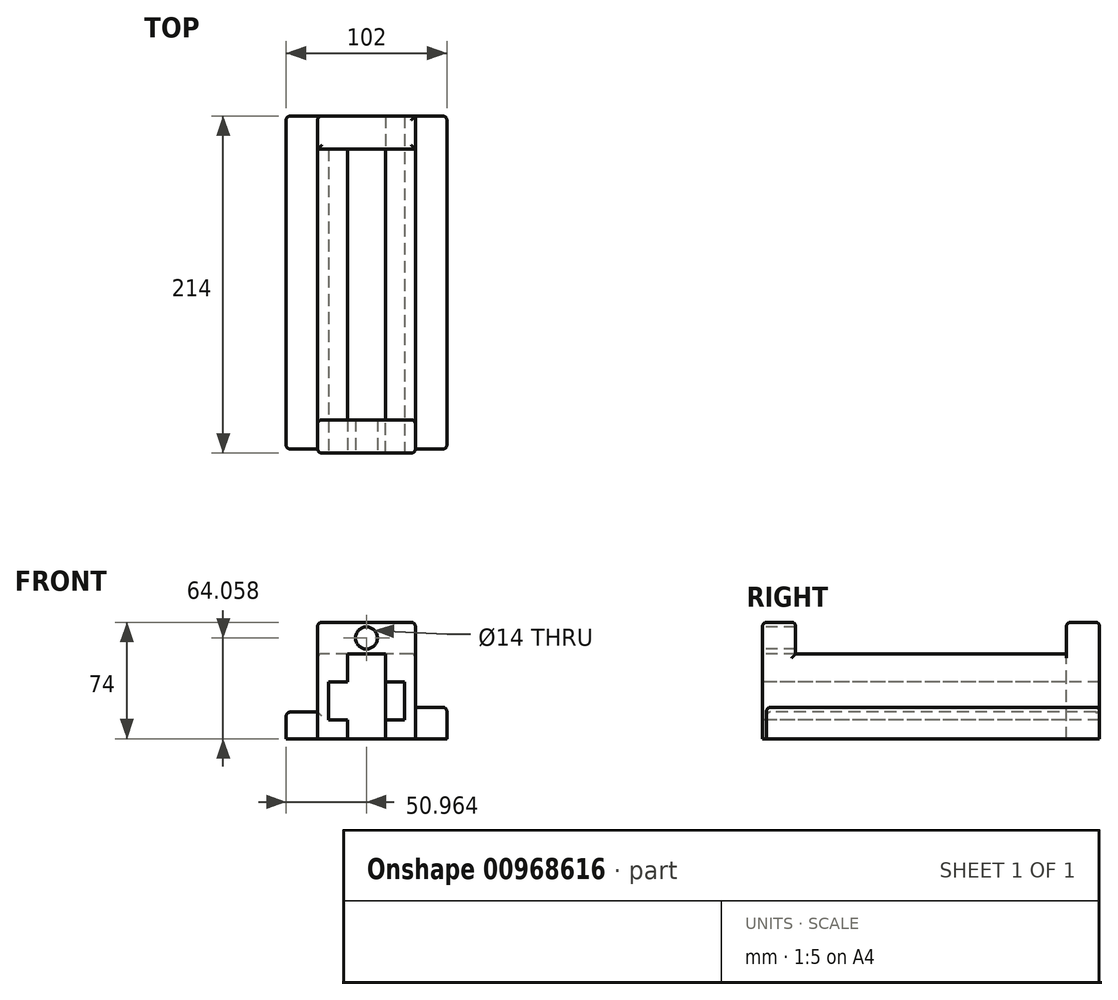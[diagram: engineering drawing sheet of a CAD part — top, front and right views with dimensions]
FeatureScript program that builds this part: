
annotation { "Feature Type Name" : "Feature", "Feature Type Description" : "" }
export const myFeature = defineFeature(function(context is Context, id is Id, definition is map)
    precondition{}
    {
        {
            var Q0;
            Q0=qCreatedBy(makeId("Front.planeOp"),FACE);
            var sketch = newSketch(context, id + "F0", { "sketchPlane" : qUnion([Q0])});
            skLineSegment(sketch, "E0", {"start": v(0, 0) * mm, "end": v(-19, 0) * mm});
            skLineSegment(sketch, "E1", {"start": v(-19, 0) * mm, "end": v(-19, 54) * mm});
            skLineSegment(sketch, "E2", {"start": v(-19, 54) * mm, "end": v(43, 54) * mm});
            skLineSegment(sketch, "E3", {"start": v(43, 54) * mm, "end": v(43, 0) * mm});
            skLineSegment(sketch, "E4", {"start": v(43, 0) * mm, "end": v(24, 0) * mm});
            skLineSegment(sketch, "E5", {"start": v(24, 0) * mm, "end": v(24, 12) * mm});
            skLineSegment(sketch, "E6", {"start": v(24, 12) * mm, "end": v(36, 12) * mm});
            skLineSegment(sketch, "E7", {"start": v(36, 12) * mm, "end": v(36, 24) * mm});
            skLineSegment(sketch, "E8", {"start": v(0, 0) * mm, "end": v(0, 12) * mm});
            skLineSegment(sketch, "E9", {"start": v(0, 12) * mm, "end": v(-12, 12) * mm});
            skLineSegment(sketch, "E10", {"start": v(-12, 12) * mm, "end": v(-12, 24) * mm});
            skLineSegment(sketch, "E11", {"start": v(-12, 24) * mm, "end": v(0, 24) * mm});
            skLineSegment(sketch, "E12", {"start": v(0, 24) * mm, "end": v(0, 36) * mm});
            skLineSegment(sketch, "E13", {"start": v(0, 36) * mm, "end": v(24, 36) * mm});
            skLineSegment(sketch, "E14", {"start": v(24, 36) * mm, "end": v(24, 24) * mm});
            skLineSegment(sketch, "E15", {"start": v(24, 24) * mm, "end": v(36, 24) * mm});
            skSolve(sketch);
        }
        {
            var Q0;
            Q0=makeQuery(id+"F0.imprint","IMPRINT",FACE,{"disambiguationData":[TD([[makeQuery(id+"F0.imprint","IMPRINT",EDGE,{"derivedFrom":sQuery(id+"F0.wireOp",EDGE,"E0")}),-1.0]])]});
            extrude(context, id + "F1", {"entities" : qUnion([Q0]), "oppositeDirection" : true, "depth" : 214 * mm, "offsetDistance" : 25 * mm});
        }
        {
            var Q0;
            Q0=makeQuery(id+"F1.opExtrude","CAP_FACE",FACE,{"disambiguationData":[OSD([sQuery(id+"F0.wireOp",EDGE,"E0"),sQuery(id+"F0.wireOp",EDGE,"E1"),sQuery(id+"F0.wireOp",EDGE,"E2"),sQuery(id+"F0.wireOp",EDGE,"E3"),sQuery(id+"F0.wireOp",EDGE,"E4"),sQuery(id+"F0.wireOp",EDGE,"E5"),sQuery(id+"F0.wireOp",EDGE,"E6"),sQuery(id+"F0.wireOp",EDGE,"E7"),sQuery(id+"F0.wireOp",EDGE,"E8"),sQuery(id+"F0.wireOp",EDGE,"E9"),sQuery(id+"F0.wireOp",EDGE,"E10"),sQuery(id+"F0.wireOp",EDGE,"E11"),sQuery(id+"F0.wireOp",EDGE,"E12"),sQuery(id+"F0.wireOp",EDGE,"E13"),sQuery(id+"F0.wireOp",EDGE,"E14"),sQuery(id+"F0.wireOp",EDGE,"E15")])],"isStart":false});
            var sketch = newSketch(context, id + "F2", { "sketchPlane" : qUnion([Q0])});
            skLineSegment(sketch, "E16.bottom", {"start": v(-24, 0) * mm, "end": v(0, 0) * mm});
            skLineSegment(sketch, "E16.top", {"start": v(-24, 36) * mm, "end": v(0, 36) * mm});
            skLineSegment(sketch, "E16.left", {"start": v(-24, 0) * mm, "end": v(-24, 36) * mm});
            skLineSegment(sketch, "E16.right", {"start": v(0, 0) * mm, "end": v(0, 36) * mm});
            skLineSegment(sketch, "E17.bottom", {"start": v(-24, 12) * mm, "end": v(-36, 12) * mm});
            skLineSegment(sketch, "E17.top", {"start": v(-24, 12) * mm, "end": v(-36, 12) * mm});
            skLineSegment(sketch, "E17.left", {"start": v(-24, 12) * mm, "end": v(-24, 12) * mm});
            skLineSegment(sketch, "E17.right", {"start": v(-36, 12) * mm, "end": v(-36, 12) * mm});
            skSolve(sketch);
        }
        {
            var Q0;
            {var subQ0=sQuery(id+"F2.wireOp",EDGE,"E17.top");Q0=makeQuery(id+"F2.imprint","IMPRINT",FACE,{"disambiguationData":[TD([[makeQuery(id+"F2.imprint","IMPRINT",EDGE,{"derivedFrom":subQ0}),-1.0]])]});}
            var Q1;
            {var subQ3=sQuery(id+"F2.wireOp",EDGE,"E16.bottom");Q1=makeQuery(id+"F2.imprint","IMPRINT",FACE,{"disambiguationData":[TD([[makeQuery(id+"F2.imprint","IMPRINT",EDGE,{"derivedFrom":subQ3}),1.0]])]});}
            var Q2;
            {var subQ1=makeQuery(id+"F1.opExtrude","CAP_EDGE",EDGE,{"disambiguationData":[OSD([sQuery(id+"F0.wireOp",EDGE,"E9")])],"isStart":false});Q2=makeQuery(id+"F2.imprint","IMPRINT",FACE,{"disambiguationData":[TD([[makeQuery(id+"F2.imprint","IMPRINT",EDGE,{"derivedFrom":subQ1}),1.0]])]});}
            extrude(context, id + "F3", {"entities" : qUnion([Q0, Q1, Q2]), "operationType" : NewBodyOperationType.ADD, "oppositeDirection" : true, "depth" : 21 * mm, "offsetDistance" : 25 * mm});
        }
        {
            var Q0;
            Q0=makeQuery(id+"F1.opExtrude","SWEPT_FACE",FACE,{"disambiguationData":[OSD([sQuery(id+"F0.wireOp",EDGE,"E2")])]});
            var sketch = newSketch(context, id + "F4", { "sketchPlane" : qUnion([Q0])});
            skLineSegment(sketch, "E18", {"start": v(43, 0) * mm, "end": v(24, 0) * mm});
            skLineSegment(sketch, "E19", {"start": v(24, 0) * mm, "end": v(24, 214) * mm});
            skLineSegment(sketch, "E20", {"start": v(-19, 0) * mm, "end": v(0, 0) * mm});
            skLineSegment(sketch, "E21", {"start": v(0, 0) * mm, "end": v(0, 214) * mm});
            skSolve(sketch);
        }
        {
            var Q0;
            {var subQ0=sQuery(id+"F4.wireOp",EDGE,"E19");Q0=makeQuery(id+"F4.imprint","IMPRINT",FACE,{"disambiguationData":[TD([[makeQuery(id+"F4.imprint","IMPRINT",EDGE,{"derivedFrom":subQ0}),1.0]])]});}
            extrude(context, id + "F5", {"entities" : qUnion([Q0]), "operationType" : NewBodyOperationType.REMOVE, "oppositeDirection" : true, "depth" : 20.2 * mm, "offsetDistance" : 25 * mm});
        }
        {
            var Q0;
            {var subQ1=sQuery(id+"F0.wireOp",EDGE,"E1");var subQ14=sQuery(id+"F0.wireOp",EDGE,"E2");Q0=makeQuery(id+"F5.boolean.opBoolean","SPLIT",FACE,{"disambiguationData":[TD([makeQuery(id+"F1.opExtrude","SWEPT_FACE",FACE,{"disambiguationData":[OSD([subQ1])]})])],"derivedFrom":makeQuery(id+"F1.opExtrude","SWEPT_FACE",FACE,{"disambiguationData":[OSD([subQ14])]})});}
            var sketch = newSketch(context, id + "F6", { "sketchPlane" : qUnion([Q0])});
            skLineSegment(sketch, "E22", {"start": v(0, 214) * mm, "end": v(0, 193) * mm});
            skLineSegment(sketch, "E23", {"start": v(0, 193) * mm, "end": v(-19, 193) * mm});
            skSolve(sketch);
        }
        {
            var Q0;
            Q0=makeQuery(id+"F5.boolean.opBoolean","COPY",FACE,{"derivedFrom":makeQuery(id+"F5.opExtrude","CAP_FACE",FACE,{"disambiguationData":[OSD([sQuery(id+"F0.wireOp",EDGE,"E2"),sQuery(id+"F4.wireOp",EDGE,"E19"),sQuery(id+"F4.wireOp",EDGE,"E21")])],"isStart":false})});
            extrude(context, id + "F7", {"entities" : qUnion([Q0]), "operationType" : NewBodyOperationType.ADD, "depth" : 40 * mm, "offsetDistance" : 25 * mm});
        }
        {
            var Q0;
            Q0=makeQuery(id+"F6.imprint","IMPRINT",FACE,{"disambiguationData":[TD([[makeQuery(id+"F6.imprint","IMPRINT",EDGE,{"derivedFrom":sQuery(id+"F6.wireOp",EDGE,"E22")}),1.0]])]});
            extrude(context, id + "F8", {"entities" : qUnion([Q0]), "operationType" : NewBodyOperationType.ADD, "depth" : 20 * mm, "offsetDistance" : 25 * mm});
        }
        {
            var Q0;
            Q0=makeQuery(id+"F7.opExtrude","SWEPT_FACE",FACE,{"disambiguationData":[OSD([sQuery(id+"F4.wireOp",EDGE,"E19")])]});
            extrude(context, id + "F9", {"entities" : qUnion([Q0]), "operationType" : NewBodyOperationType.ADD, "depth" : 19 * mm, "offsetDistance" : 25 * mm});
        }
        {
            var Q0;
            Q0=makeQuery(id+"F1.opExtrude","SWEPT_FACE",FACE,{"disambiguationData":[OSD([sQuery(id+"F0.wireOp",EDGE,"E11")])]});
            var Q1;
            Q1=makeQuery(id+"F1.opExtrude","SWEPT_FACE",FACE,{"disambiguationData":[OSD([sQuery(id+"F0.wireOp",EDGE,"E15")])]});
            extrude(context, id + "F10", {"entities" : qUnion([Q0, Q1]), "operationType" : NewBodyOperationType.REMOVE, "oppositeDirection" : true, "depth" : 12 * mm, "offsetDistance" : 25 * mm});
        }
        {
            var Q0;
            {var subQ1=sQuery(id+"F0.wireOp",EDGE,"E1");var subQ14=sQuery(id+"F0.wireOp",EDGE,"E2");Q0=makeQuery(id+"F5.boolean.opBoolean","SPLIT",FACE,{"disambiguationData":[TD([makeQuery(id+"F1.opExtrude","SWEPT_FACE",FACE,{"disambiguationData":[OSD([subQ1])]})])],"derivedFrom":makeQuery(id+"F1.opExtrude","SWEPT_FACE",FACE,{"disambiguationData":[OSD([subQ14])]})});}
            var sketch = newSketch(context, id + "F11", { "sketchPlane" : qUnion([Q0])});
            skLineSegment(sketch, "E24", {"start": v(-19, 0) * mm, "end": v(-19, 21) * mm});
            skLineSegment(sketch, "E25", {"start": v(-19, 21) * mm, "end": v(0, 21) * mm});
            skSolve(sketch);
        }
        {
            var Q0;
            Q0=makeQuery(id+"F11.imprint","IMPRINT",FACE,{"disambiguationData":[TD([[makeQuery(id+"F11.imprint","IMPRINT",EDGE,{"derivedFrom":sQuery(id+"F11.wireOp",EDGE,"E24")}),1.0]])]});
            extrude(context, id + "F12", {"entities" : qUnion([Q0]), "operationType" : NewBodyOperationType.ADD, "depth" : 20 * mm, "offsetDistance" : 25 * mm});
        }
        {
            var Q0;
            {var subQ0=sQuery(id+"F4.wireOp",EDGE,"E19");Q0=makeQuery(id+"F9.boolean.opBoolean","MERGE",FACE,{"derivedFrom":[makeQuery(id+"F7.opExtrude","CAP_FACE",FACE,{"disambiguationData":[OSD([sQuery(id+"F0.wireOp",EDGE,"E2"),subQ0,sQuery(id+"F4.wireOp",EDGE,"E21")])],"isStart":false}),makeQuery(id+"F9.opExtrude","SWEPT_FACE",FACE,{"disambiguationData":[OSD([subQ0]),TDD([makeQuery(id+"F7.opExtrude","CAP_EDGE",EDGE,{"disambiguationData":[OSD([subQ0])],"isStart":false})])]})]});}
            extrude(context, id + "F13", {"entities" : qUnion([Q0]), "operationType" : NewBodyOperationType.ADD, "depth" : 0.2 * mm, "offsetDistance" : 25 * mm});
        }
        {
            var Q0;
            {var subQ0=sQuery(id+"F4.wireOp",EDGE,"E21");Q0=makeQuery(id+"F12.boolean.opBoolean","MERGE",FACE,{"derivedFrom":[makeQuery(id+"F5.boolean.opBoolean","MERGE",FACE,{"derivedFrom":[makeQuery(id+"F1.opExtrude","SWEPT_FACE",FACE,{"disambiguationData":[OSD([sQuery(id+"F0.wireOp",EDGE,"E12")])]})],"fromTools":[makeQuery(id+"F5.opExtrude","SWEPT_FACE",FACE,{"disambiguationData":[OSD([subQ0])]})]}),makeQuery(id+"F12.opExtrude","SWEPT_FACE",FACE,{"disambiguationData":[OSD([subQ0])]})]});}
            var sketch = newSketch(context, id + "F14", { "sketchPlane" : qUnion([Q0])});
            skLineSegment(sketch, "E26", {"start": v(21, 54) * mm, "end": v(0, 54) * mm});
            skSolve(sketch);
        }
        {
            var Q0;
            {var subQ0=sQuery(id+"F14.wireOp",EDGE,"E26");Q0=makeQuery(id+"F14.imprint","IMPRINT",FACE,{"disambiguationData":[TD([[makeQuery(id+"F14.imprint","IMPRINT",EDGE,{"derivedFrom":subQ0}),-1.0]])]});}
            extrude(context, id + "F15", {"entities" : qUnion([Q0]), "operationType" : NewBodyOperationType.ADD, "depth" : 43 * mm, "offsetDistance" : 25 * mm});
        }
        {
            var Q0;
            {var subQ0=sQuery(id+"F4.wireOp",EDGE,"E21");var subQ1=sQuery(id+"F0.wireOp",EDGE,"E12");var subQ2=sQuery(id+"F0.wireOp",EDGE,"E2");var subQ3=sQuery(id+"F0.wireOp",EDGE,"E11");var subQ6=sQuery(id+"F0.wireOp",EDGE,"E10");var subQ7=sQuery(id+"F0.wireOp",EDGE,"E8");var subQ8=sQuery(id+"F0.wireOp",EDGE,"E9");var subQ9=sQuery(id+"F0.wireOp",EDGE,"E0");var subQ11=sQuery(id+"F0.wireOp",EDGE,"E1");var subQ12=sQuery(id+"F0.wireOp",EDGE,"E4");var subQ14=sQuery(id+"F0.wireOp",EDGE,"E15");var subQ15=sQuery(id+"F0.wireOp",EDGE,"E14");var subQ16=sQuery(id+"F0.wireOp",EDGE,"E7");var subQ17=sQuery(id+"F0.wireOp",EDGE,"E6");var subQ18=sQuery(id+"F0.wireOp",EDGE,"E5");var subQ19=sQuery(id+"F0.wireOp",EDGE,"E3");var subQ20=makeQuery(id+"F1.opExtrude","CAP_FACE",FACE,{"disambiguationData":[OSD([subQ9,subQ11,subQ2,subQ19,subQ12,subQ18,subQ17,subQ16,subQ7,subQ8,subQ6,subQ3,subQ1,sQuery(id+"F0.wireOp",EDGE,"E13"),subQ15,subQ14])],"isStart":true});Q0=makeQuery(id+"F15.boolean.opBoolean","MERGE",FACE,{"derivedFrom":[makeQuery(id+"F5.boolean.opBoolean","SPLIT",FACE,{"disambiguationData":[TD([makeQuery(id+"F1.opExtrude","SWEPT_FACE",FACE,{"disambiguationData":[OSD([subQ19])]})])],"derivedFrom":subQ20}),makeQuery(id+"F12.boolean.opBoolean","MERGE",FACE,{"derivedFrom":[makeQuery(id+"F5.boolean.opBoolean","SPLIT",FACE,{"disambiguationData":[TD([makeQuery(id+"F1.opExtrude","SWEPT_FACE",FACE,{"disambiguationData":[OSD([subQ11])]})])],"derivedFrom":subQ20}),makeQuery(id+"F12.opExtrude","SWEPT_FACE",FACE,{"disambiguationData":[OSD([subQ2])]})]}),makeQuery(id+"F15.opExtrude","SWEPT_FACE",FACE,{"disambiguationData":[OSD([subQ2,subQ1,sQuery(id+"F4.wireOp",EDGE,"E20"),subQ0])]})]});}
            var sketch = newSketch(context, id + "F16", { "sketchPlane" : qUnion([Q0])});
            skSolve(sketch);
        }
        {
            var Q0;
            {var subQ1=sQuery(id+"F0.wireOp",EDGE,"E2");var subQ5=sQuery(id+"F4.wireOp",EDGE,"E21");var subQ6=sQuery(id+"F4.wireOp",EDGE,"E20");var subQ7=sQuery(id+"F0.wireOp",EDGE,"E12");var subQ13=makeQuery(id+"F15.boolean.opBoolean","MERGE",EDGE,{"derivedFrom":[makeQuery(id+"F12.opExtrude","CAP_EDGE",EDGE,{"disambiguationData":[OSD([subQ1])],"isStart":false}),makeQuery(id+"F15.opExtrude","SWEPT_EDGE",EDGE,{"disambiguationData":[OSD([subQ1,subQ7,subQ6,subQ5])]})]});Q0=makeQuery(id+"F16.imprint","IMPRINT",FACE,{"disambiguationData":[TD([[makeQuery(id+"F16.imprint","IMPRINT",EDGE,{"derivedFrom":subQ13}),-1.0]])]});}
            var sketch = newSketch(context, id + "F17", { "sketchPlane" : qUnion([Q0])});
            skCircle(sketch, "E27", {"center": v(11.96, 64.06) * mm, "radius": 7 * mm});
            skSolve(sketch);
        }
        {
            var Q0;
            Q0=makeQuery(id+"F17.imprint","IMPRINT",FACE,{"disambiguationData":[TD([[makeQuery(id+"F17.imprint","IMPRINT",EDGE,{"derivedFrom":sQuery(id+"F17.wireOp",EDGE,"E27")}),1.0]])]});
            extrude(context, id + "F18", {"entities" : qUnion([Q0]), "operationType" : NewBodyOperationType.REMOVE, "oppositeDirection" : true, "depth" : 69.1 * mm, "offsetDistance" : 25 * mm});
        }
        {
            var Q0;
            Q0=makeQuery(id+"F16.imprint","IMPRINT",FACE,{"disambiguationData":[TD([[makeQuery(id+"F16.imprint","IMPRINT",EDGE,{"derivedFrom":makeQuery(id+"F1.opExtrude","CAP_EDGE",EDGE,{"disambiguationData":[OSD([sQuery(id+"F0.wireOp",EDGE,"E0")])],"isStart":true})}),-1.0]])]});
            var sketch = newSketch(context, id + "F19", { "sketchPlane" : qUnion([Q0])});
            skSolve(sketch);
        }
        {
            var Q0;
            Q0=makeQuery(id+"F1.opExtrude","SWEPT_EDGE",EDGE,{"disambiguationData":[OSD([sQuery(id+"F0.wireOp",EDGE,"E1"),sQuery(id+"F0.wireOp",EDGE,"E2")])]});
            var Q1;
            Q1=makeQuery(id+"F1.opExtrude","SWEPT_EDGE",EDGE,{"disambiguationData":[OSD([sQuery(id+"F0.wireOp",EDGE,"E2"),sQuery(id+"F0.wireOp",EDGE,"E3")])]});
            var Q2;
            {var subQ0=sQuery(id+"F0.wireOp",EDGE,"E2");Q2=makeQuery(id+"F15.boolean.opBoolean","MERGE",EDGE,{"derivedFrom":[makeQuery(id+"F12.opExtrude","CAP_EDGE",EDGE,{"disambiguationData":[OSD([subQ0])],"isStart":false}),makeQuery(id+"F15.opExtrude","SWEPT_EDGE",EDGE,{"disambiguationData":[OSD([subQ0,sQuery(id+"F0.wireOp",EDGE,"E12"),sQuery(id+"F4.wireOp",EDGE,"E20"),sQuery(id+"F4.wireOp",EDGE,"E21")])]})]});}
            var Q3;
            Q3=makeQuery(id+"F13.boolean.opBoolean","MERGE",EDGE,{"derivedFrom":[makeQuery(id+"F8.opExtrude","CAP_EDGE",EDGE,{"disambiguationData":[OSD([sQuery(id+"F6.wireOp",EDGE,"E23")])],"isStart":false}),makeQuery(id+"F13.opExtrude","CAP_EDGE",EDGE,{"disambiguationData":[OSD([sQuery(id+"F0.wireOp",EDGE,"E2"),sQuery(id+"F0.wireOp",EDGE,"E7"),sQuery(id+"F0.wireOp",EDGE,"E9"),sQuery(id+"F0.wireOp",EDGE,"E10"),sQuery(id+"F0.wireOp",EDGE,"E11"),sQuery(id+"F0.wireOp",EDGE,"E15"),sQuery(id+"F2.wireOp",EDGE,"E16.bottom"),sQuery(id+"F2.wireOp",EDGE,"E16.top"),sQuery(id+"F2.wireOp",EDGE,"E16.left"),sQuery(id+"F2.wireOp",EDGE,"E16.right"),sQuery(id+"F2.wireOp",EDGE,"E17.top"),sQuery(id+"F4.wireOp",EDGE,"E19"),sQuery(id+"F4.wireOp",EDGE,"E21")])],"isStart":false})]});
            var Q4;
            {var subQ0=sQuery(id+"F0.wireOp",EDGE,"E2");Q4=makeQuery(id+"F13.boolean.opBoolean","MERGE",EDGE,{"derivedFrom":[makeQuery(id+"F8.opExtrude","CAP_EDGE",EDGE,{"disambiguationData":[OSD([subQ0])],"isStart":false}),makeQuery(id+"F13.opExtrude","CAP_EDGE",EDGE,{"disambiguationData":[OSD([subQ0,sQuery(id+"F4.wireOp",EDGE,"E19")])],"isStart":false})]});}
            var Q5;
            Q5=makeQuery(id+"F8.opExtrude","CAP_EDGE",EDGE,{"disambiguationData":[OSD([sQuery(id+"F0.wireOp",EDGE,"E1"),sQuery(id+"F0.wireOp",EDGE,"E2")])],"isStart":false});
            var Q6;
            Q6=makeQuery(id+"F13.opExtrude","CAP_EDGE",EDGE,{"disambiguationData":[OSD([sQuery(id+"F4.wireOp",EDGE,"E19")])],"isStart":false});
            var Q7;
            Q7=makeQuery(id+"F15.boolean.opBoolean","MERGE",EDGE,{"derivedFrom":[makeQuery(id+"F1.opExtrude","CAP_EDGE",EDGE,{"disambiguationData":[OSD([sQuery(id+"F0.wireOp",EDGE,"E3")])],"isStart":true}),makeQuery(id+"F15.opExtrude","CAP_EDGE",EDGE,{"disambiguationData":[OSD([sQuery(id+"F0.wireOp",EDGE,"E2"),sQuery(id+"F0.wireOp",EDGE,"E12"),sQuery(id+"F4.wireOp",EDGE,"E20"),sQuery(id+"F4.wireOp",EDGE,"E21")])],"isStart":false})]});
            var Q8;
            Q8=makeQuery(id+"F12.boolean.opBoolean","MERGE",EDGE,{"derivedFrom":[makeQuery(id+"F1.opExtrude","CAP_EDGE",EDGE,{"disambiguationData":[OSD([sQuery(id+"F0.wireOp",EDGE,"E1")])],"isStart":true}),makeQuery(id+"F12.opExtrude","SWEPT_EDGE",EDGE,{"disambiguationData":[OSD([sQuery(id+"F0.wireOp",EDGE,"E2"),sQuery(id+"F11.wireOp",EDGE,"E24")])]})]});
            var Q9;
            {var subQ0=sQuery(id+"F11.wireOp",EDGE,"E25");Q9=makeQuery(id+"F15.boolean.opBoolean","MERGE",EDGE,{"derivedFrom":[makeQuery(id+"F12.opExtrude","CAP_EDGE",EDGE,{"disambiguationData":[OSD([subQ0])],"isStart":false}),makeQuery(id+"F15.opExtrude","SWEPT_EDGE",EDGE,{"disambiguationData":[OSD([sQuery(id+"F4.wireOp",EDGE,"E21"),subQ0])]})]});}
            fillet(context, id + "F20", {"entities" : qUnion([Q0, Q1, Q2, Q3, Q4, Q5, Q6, Q7, Q8, Q9]), "radius" : 2.5 * mm, "tangentPropagation" : true, "allowEdgeOverflow" : false});
        }
        {
            var Q0;
            Q0=makeQuery(id+"F12.opExtrude","CAP_EDGE",EDGE,{"disambiguationData":[OSD([sQuery(id+"F11.wireOp",EDGE,"E24")])],"isStart":false});
            var Q1;
            Q1=makeQuery(id+"F15.opExtrude","CAP_EDGE",EDGE,{"disambiguationData":[OSD([sQuery(id+"F4.wireOp",EDGE,"E21")])],"isStart":false});
            fillet(context, id + "F21", {"entities" : qUnion([Q0, Q1]), "radius" : 2.5 * mm, "tangentPropagation" : true, "allowEdgeOverflow" : false});
        }
        {
            var Q0;
            {var subQ0=sQuery(id+"F0.wireOp",EDGE,"E1");Q0=makeQuery(id+"F12.boolean.opBoolean","MERGE",FACE,{"derivedFrom":[makeQuery(id+"F8.boolean.opBoolean","MERGE",FACE,{"derivedFrom":[makeQuery(id+"F1.opExtrude","SWEPT_FACE",FACE,{"disambiguationData":[OSD([subQ0])]}),makeQuery(id+"F8.opExtrude","SWEPT_FACE",FACE,{"disambiguationData":[OSD([subQ0,sQuery(id+"F0.wireOp",EDGE,"E2")])]})]}),makeQuery(id+"F12.opExtrude","SWEPT_FACE",FACE,{"disambiguationData":[OSD([sQuery(id+"F11.wireOp",EDGE,"E24")])]})]});}
            var sketch = newSketch(context, id + "F22", { "sketchPlane" : qUnion([Q0])});
            skLineSegment(sketch, "E28", {"start": v(-214, 0) * mm, "end": v(-214, 16.95) * mm});
            skLineSegment(sketch, "E29", {"start": v(-214, 16.95) * mm, "end": v(-2.5, 16.95) * mm});
            skLineSegment(sketch, "E30", {"start": v(-2.5, 16.95) * mm, "end": v(-2.5, 0) * mm});
            skLineSegment(sketch, "E31", {"start": v(-2.5, 0) * mm, "end": v(-214, 0) * mm});
            skSolve(sketch);
        }
        {
            var Q0;
            Q0=makeQuery(id+"F22.imprint","IMPRINT",FACE,{"disambiguationData":[TD([[makeQuery(id+"F22.imprint","IMPRINT",EDGE,{"derivedFrom":sQuery(id+"F22.wireOp",EDGE,"E28")}),-1.0]])]});
            extrude(context, id + "F23", {"entities" : qUnion([Q0]), "operationType" : NewBodyOperationType.ADD, "depth" : 20 * mm, "offsetDistance" : 25 * mm});
        }
        {
            var Q0;
            {var subQ0=sQuery(id+"F0.wireOp",EDGE,"E1");Q0=makeQuery(id+"F8.boolean.opBoolean","MERGE",EDGE,{"derivedFrom":[makeQuery(id+"F1.opExtrude","CAP_EDGE",EDGE,{"disambiguationData":[OSD([subQ0])],"isStart":false}),makeQuery(id+"F8.opExtrude","SWEPT_EDGE",EDGE,{"disambiguationData":[OSD([subQ0,sQuery(id+"F0.wireOp",EDGE,"E2")])]})]});}
            var Q1;
            Q1=makeQuery(id+"F23.opExtrude","SWEPT_EDGE",EDGE,{"disambiguationData":[OSD([sQuery(id+"F0.wireOp",EDGE,"E1"),sQuery(id+"F0.wireOp",EDGE,"E2"),sQuery(id+"F22.wireOp",EDGE,"E28"),sQuery(id+"F22.wireOp",EDGE,"E29")])]});
            var Q2;
            Q2=makeQuery(id+"F23.opExtrude","CAP_EDGE",EDGE,{"disambiguationData":[OSD([sQuery(id+"F22.wireOp",EDGE,"E28")])],"isStart":false});
            var Q3;
            Q3=makeQuery(id+"F23.opExtrude","CAP_EDGE",EDGE,{"disambiguationData":[OSD([sQuery(id+"F22.wireOp",EDGE,"E29")])],"isStart":false});
            var Q4;
            Q4=makeQuery(id+"F23.opExtrude","SWEPT_EDGE",EDGE,{"disambiguationData":[OSD([sQuery(id+"F0.wireOp",EDGE,"E1"),sQuery(id+"F0.wireOp",EDGE,"E2"),sQuery(id+"F11.wireOp",EDGE,"E24"),sQuery(id+"F22.wireOp",EDGE,"E29"),sQuery(id+"F22.wireOp",EDGE,"E30")])]});
            var Q5;
            Q5=makeQuery(id+"F23.opExtrude","CAP_EDGE",EDGE,{"disambiguationData":[OSD([sQuery(id+"F22.wireOp",EDGE,"E30")])],"isStart":false});
            fillet(context, id + "F24", {"entities" : qUnion([Q0, Q1, Q2, Q3, Q4, Q5]), "radius" : 2.5 * mm, "tangentPropagation" : true, "allowEdgeOverflow" : false});
        }
        {
            var Q0;
            {var subQ0=sQuery(id+"F4.wireOp",EDGE,"E19");Q0=makeQuery(id+"F15.boolean.opBoolean","MERGE",FACE,{"derivedFrom":[makeQuery(id+"F13.boolean.opBoolean","MERGE",FACE,{"derivedFrom":[makeQuery(id+"F9.boolean.opBoolean","MERGE",FACE,{"derivedFrom":[makeQuery(id+"F1.opExtrude","SWEPT_FACE",FACE,{"disambiguationData":[OSD([sQuery(id+"F0.wireOp",EDGE,"E3")])]}),makeQuery(id+"F9.opExtrude","CAP_FACE",FACE,{"disambiguationData":[OSD([subQ0])],"isStart":false})]}),makeQuery(id+"F13.opExtrude","SWEPT_FACE",FACE,{"disambiguationData":[OSD([subQ0])]})]}),makeQuery(id+"F15.opExtrude","CAP_FACE",FACE,{"disambiguationData":[OSD([sQuery(id+"F0.wireOp",EDGE,"E2"),sQuery(id+"F0.wireOp",EDGE,"E12"),sQuery(id+"F4.wireOp",EDGE,"E20"),sQuery(id+"F4.wireOp",EDGE,"E21"),sQuery(id+"F11.wireOp",EDGE,"E25"),sQuery(id+"F14.wireOp",EDGE,"E26")])],"isStart":false})]});}
            var sketch = newSketch(context, id + "F25", { "sketchPlane" : qUnion([Q0])});
            skLineSegment(sketch, "E32", {"start": v(2.5, 0) * mm, "end": v(2.5, 20) * mm});
            skLineSegment(sketch, "E33", {"start": v(2.5, 20) * mm, "end": v(214, 20) * mm});
            skLineSegment(sketch, "E34", {"start": v(214, 20) * mm, "end": v(214, 0) * mm});
            skLineSegment(sketch, "E35", {"start": v(214, 0) * mm, "end": v(2.5, 0) * mm});
            skSolve(sketch);
        }
        {
            var Q0;
            Q0=makeQuery(id+"F25.imprint","IMPRINT",FACE,{"disambiguationData":[TD([[makeQuery(id+"F25.imprint","IMPRINT",EDGE,{"derivedFrom":sQuery(id+"F25.wireOp",EDGE,"E32")}),1.0]])]});
            extrude(context, id + "F26", {"entities" : qUnion([Q0]), "operationType" : NewBodyOperationType.ADD, "depth" : 20 * mm, "offsetDistance" : 25 * mm});
        }
        {
            var Q0;
            Q0=makeQuery(id+"F26.opExtrude","SWEPT_EDGE",EDGE,{"disambiguationData":[OSD([sQuery(id+"F0.wireOp",EDGE,"E2"),sQuery(id+"F0.wireOp",EDGE,"E3"),sQuery(id+"F0.wireOp",EDGE,"E12"),sQuery(id+"F4.wireOp",EDGE,"E19"),sQuery(id+"F4.wireOp",EDGE,"E20"),sQuery(id+"F4.wireOp",EDGE,"E21"),sQuery(id+"F11.wireOp",EDGE,"E25"),sQuery(id+"F14.wireOp",EDGE,"E26"),sQuery(id+"F25.wireOp",EDGE,"E32"),sQuery(id+"F25.wireOp",EDGE,"E33")])]});
            var Q1;
            Q1=makeQuery(id+"F26.opExtrude","CAP_EDGE",EDGE,{"disambiguationData":[OSD([sQuery(id+"F25.wireOp",EDGE,"E33")])],"isStart":false});
            var Q2;
            Q2=makeQuery(id+"F26.opExtrude","CAP_EDGE",EDGE,{"disambiguationData":[OSD([sQuery(id+"F25.wireOp",EDGE,"E32")])],"isStart":false});
            var Q3;
            Q3=makeQuery(id+"F26.opExtrude","SWEPT_EDGE",EDGE,{"disambiguationData":[OSD([sQuery(id+"F0.wireOp",EDGE,"E2"),sQuery(id+"F0.wireOp",EDGE,"E3"),sQuery(id+"F4.wireOp",EDGE,"E19"),sQuery(id+"F25.wireOp",EDGE,"E33"),sQuery(id+"F25.wireOp",EDGE,"E34")])]});
            var Q4;
            Q4=makeQuery(id+"F26.opExtrude","CAP_EDGE",EDGE,{"disambiguationData":[OSD([sQuery(id+"F25.wireOp",EDGE,"E34")])],"isStart":false});
            fillet(context, id + "F27", {"entities" : qUnion([Q0, Q1, Q2, Q3, Q4]), "radius" : 2.5 * mm, "tangentPropagation" : true, "allowEdgeOverflow" : false});
        }
    });
